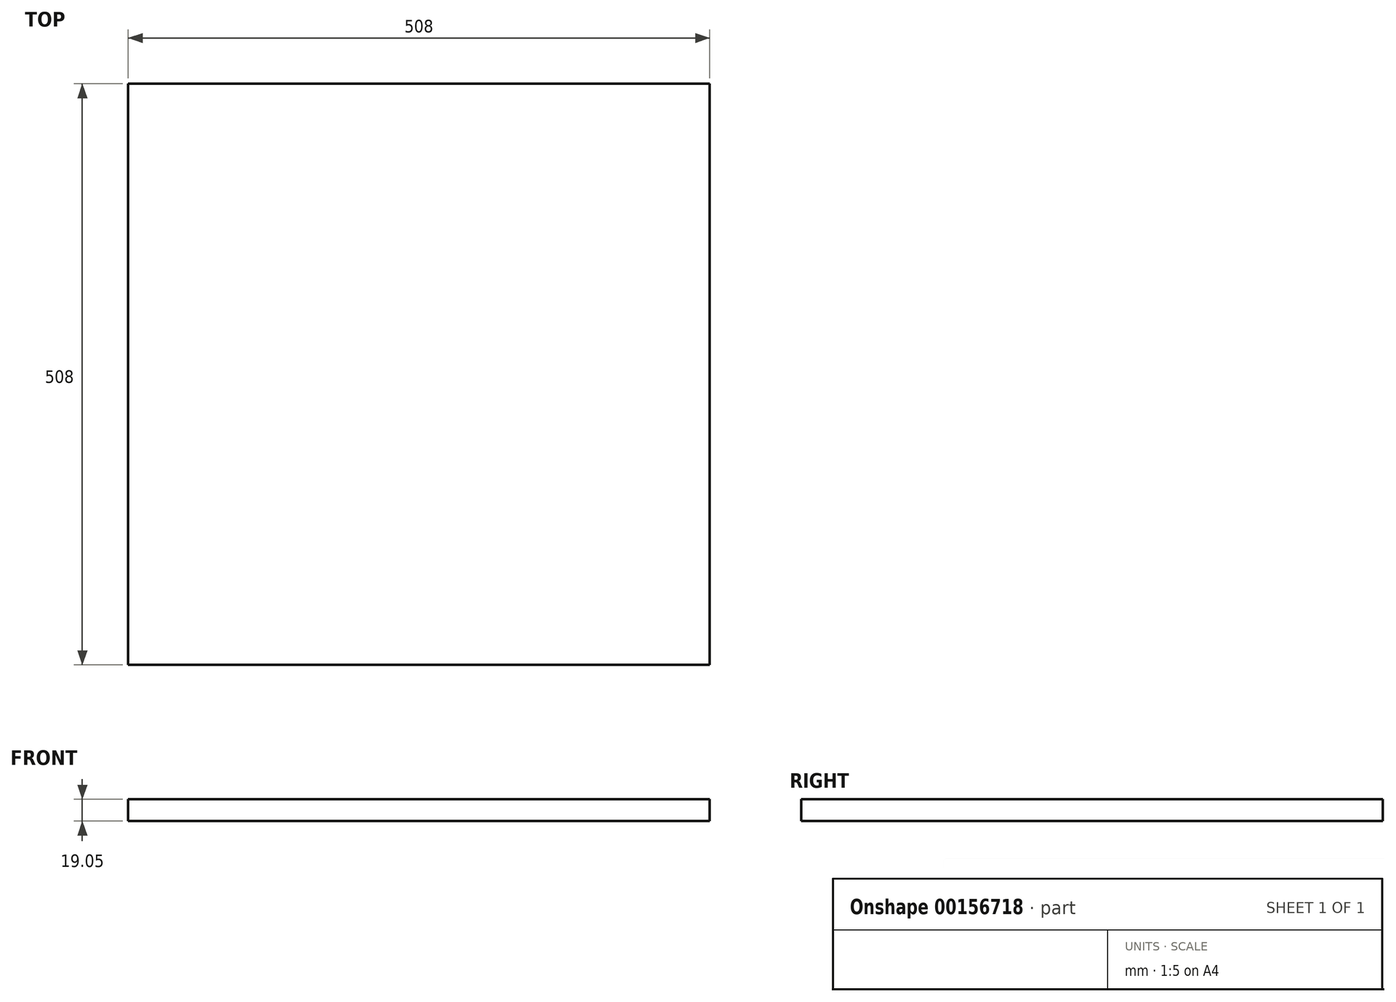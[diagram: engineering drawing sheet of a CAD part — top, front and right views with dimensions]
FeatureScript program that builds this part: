
annotation { "Feature Type Name" : "Feature", "Feature Type Description" : "" }
export const myFeature = defineFeature(function(context is Context, id is Id, definition is map)
    precondition{}
    {
        {
            var Q0;
            Q0=qCreatedBy(makeId("Front.planeOp"),FACE);
            var sketch = newSketch(context, id + "F0", { "sketchPlane" : qUnion([Q0])});
            skLineSegment(sketch, "E0.bottom", {"start": v(-305.84, 49.92) * mm, "end": v(202.16, 49.92) * mm});
            skLineSegment(sketch, "E0.top", {"start": v(-305.84, 30.87) * mm, "end": v(202.16, 30.87) * mm});
            skLineSegment(sketch, "E0.left", {"start": v(-305.84, 49.92) * mm, "end": v(-305.84, 30.87) * mm});
            skLineSegment(sketch, "E0.right", {"start": v(202.16, 49.92) * mm, "end": v(202.16, 30.87) * mm});
            skSolve(sketch);
        }
        {
            var Q0;
            Q0=sQuery(id+"F0.wireOp",EDGE,"E0.bottom");
            var Q1;
            Q1=sQuery(id+"F0.wireOp",EDGE,"E0.top");
            var Q2;
            Q2=sQuery(id+"F0.wireOp",EDGE,"E0.left");
            var Q3;
            Q3=sQuery(id+"F0.wireOp",EDGE,"E0.right");
            extrude(context, id + "F1", {"bodyType" : ToolBodyType.SURFACE, "surfaceEntities" : qUnion([Q0, Q1, Q2, Q3]), "depth" : 508 * mm});
        }
    });
